# Revit family: Mi-NEUT-FINAL
name_source: partatom
category: Plumbing Fixtures
revit_build: Autodesk Revit 2015 (Build: 20140322_1515(x64)
units: mm (PartAtom-declared; Revit-internal decimal feet)

## types (22) — shared parameters
RAD = 0' - 5 1/2"

## per-type parameters (varying)
| type | A | B | C | D | E | ID | Length | Neut | Neut-2 | OD | Wide | c |
| MI-NEUT-5 | 0' - 11" | 1' - 3 5/8" | 0' - 11" | 0' - 8" | 0' - 2" | 0' - 1 15/16" | 6' - 10 11/16" | Yes | No | 0' - 3 1/2" | 4' - 9 7/16" | 0' - 5 17/32" |
| MI-NEUT-15 | 1' - 6" | 1' - 9 5/8" | 0' - 11" | 0' - 8" | 0' - 2" | 0' - 1 15/16" | 6' - 10 11/16" | Yes | No | 0' - 3 1/2" | 4' - 9 7/16" | 0' - 5 17/32" |
| MI-NEUT-30 | 1' - 6" | 2' - 5 5/8" | 1' - 11" | 1' - 7" | 0' - 3" | 0' - 2 15/16" | 6' - 10 11/16" | Yes | No | 0' - 4 1/2" | 4' - 9 7/16" | 0' - 5 17/32" |
| MI-NEUT-55 | 1' - 10" | 3' - 0 5/8" | 2' - 3" | 1' - 11" | 0' - 4" | 0' - 3 15/16" | 6' - 10 11/16" | Yes | No | 0' - 5 1/2" | 4' - 9 7/16" | 0' - 5 17/32" |
| MI-NEUT-100 | 2' - 4" | 3' - 7 1/4" | 2' - 11" | 2' - 7" | 0' - 4" | 0' - 3 15/16" | 6' - 10 11/16" | Yes | No | 0' - 5 1/2" | 4' - 9 7/16" | 0' - 5 17/32" |
| MI-NEUT-150 | 2' - 7" | 4' - 1 7/8" | 3' - 2" | 2' - 10" | 0' - 4" | 0' - 3 15/16" | 6' - 10 11/16" | Yes | No | 0' - 5 1/2" | 4' - 9 7/16" | 0' - 5 17/32" |
| MI-NEUT-175 | 2' - 6" | 5' - 2 3/4" | 3' - 10" | 3' - 6" | 0' - 4" | 0' - 3 15/16" | 6' - 10 11/16" | Yes | No | 0' - 5 1/2" | 4' - 9 7/16" | 0' - 5 17/32" |
| MI-NEUT-200 | 3' - 0" | 4' - 1 3/4" | 3' - 2" | 2' - 10" | 0' - 6" | 0' - 5 15/16" | 6' - 10 11/16" | Yes | No | 0' - 7 1/2" | 4' - 9 7/16" | 0' - 5 17/32" |
| MI-NEUT-275 | 3' - 6" | 4' - 1" | 3' - 2" | 2' - 10" | 0' - 6" | 0' - 5 15/16" | 6' - 10 11/16" | Yes | No | 0' - 7 1/2" | 4' - 9 7/16" | 0' - 5 17/32" |
| MI-NEUT-300 | 4' - 0" | 3' - 6 1/4" | 3' - 0 1/4" | 2' - 8 1/4" | 0' - 6" | 0' - 5 15/16" | 6' - 10 11/16" | Yes | No | 0' - 7 1/2" | 4' - 9 7/16" | 0' - 5 17/32" |
| MI-NEUT-350 | 4' - 0" | 4' - 1 1/4" | 3' - 2" | 2' - 10" | 0' - 6" | 0' - 5 15/16" | 6' - 10 11/16" | Yes | No | 0' - 7 1/2" | 4' - 9 7/16" | 0' - 5 17/32" |
| MI-NEUT-500 | 4' - 4" | 5' - 2 1/8" | 4' - 4" | 3' - 10" | 0' - 6" | 0' - 5 15/16" | 6' - 10 11/16" | Yes | No | 0' - 7 1/2" | 4' - 9 7/16" | 0' - 5 17/32" |
| MI-NEUT-550 | 4' - 0" | 6' - 1" | 5' - 4" | 5' - 0" | 0' - 6" | 0' - 5 15/16" | 6' - 10 11/16" | Yes | No | 0' - 7 1/2" | 4' - 9 7/16" | 0' - 5 17/32" |
| MI-NEUT-650 | 4' - 0" | 7' - 1 1/4" | 6' - 5" | 6' - 1" | 0' - 6" | 0' - 5 15/16" | 6' - 10 11/16" | Yes | No | 0' - 7 1/2" | 4' - 9 7/16" | 0' - 5 17/32" |
| MI-NEUT-700 | 4' - 7" | 6' - 2 1/4" | 5' - 2" | 4' - 10" | 0' - 6" | 0' - 5 15/16" | 6' - 10 11/16" | Yes | No | 0' - 7 1/2" | 4' - 9 7/16" | 0' - 5 17/32" |
| MI-NEUT-800 | 5' - 0" | 5' - 8" | 4' - 9" | 4' - 5" | 0' - 6" | 0' - 5 15/16" | 6' - 10 11/16" | Yes | No | 0' - 7 1/2" | 4' - 9 7/16" | 0' - 5 17/32" |
| MI-NEUT-1000 | 5' - 6" | 6' - 2 1/2" | 5' - 4" | 5' - 0" | 0' - 6" | 0' - 5 15/16" | 6' - 10 11/16" | Yes | No | 0' - 7 1/2" | 4' - 9 7/16" | 0' - 5 17/32" |
| MI-NEUT-1200 | 5' - 9" | 7' - 2 7/8" | 6' - 2" | 5' - 8" | 0' - 6" | 0' - 5 15/16" | 6' - 10 11/16" | Yes | No | 0' - 7 1/2" | 4' - 9 7/16" | 0' - 5 17/32" |
| MI-NEUT-1500 | 6' - 1" | 7' - 1 3/8" | 6' - 2" | 5' - 8" | 0' - 6" | 0' - 5 15/16" | 6' - 10 11/16" | Yes | No | 0' - 7 1/2" | 4' - 9 7/16" | 0' - 5 17/32" |
| MI-NEUT-2000 | 7' - 0" | 7' - 8 1/8" | 6' - 2" | 5' - 8" | 0' - 6" | 0' - 5 15/16" | 6' - 10 11/16" | Yes | No | 0' - 7 1/2" | 4' - 9 7/16" | 0' - 5 17/32" |
| MI-NEUT-3000 | 7' - 11" | 8' - 4" | 7' - 3" | 6' - 9" | 0' - 6" | 0' - 5 15/16" | 6' - 10 11/16" | Yes | No | 0' - 7 1/2" | 4' - 9 7/16" | 0' - 5 17/32" |
| MI-NEUT-2 | 2' - 4" | 3' - 7 1/4" | 2' - 11" | 2' - 7" | 0' - 4" | 0' - 3 15/16" | 1' - 1 3/4" | No | Yes | 0' - 5 1/2" | 0' - 11 1/8" | 0' - 6 1/2" |

## geometry (parser evidence)
native form markers: Sweep x5
no freeform markers — native parametric forms only
